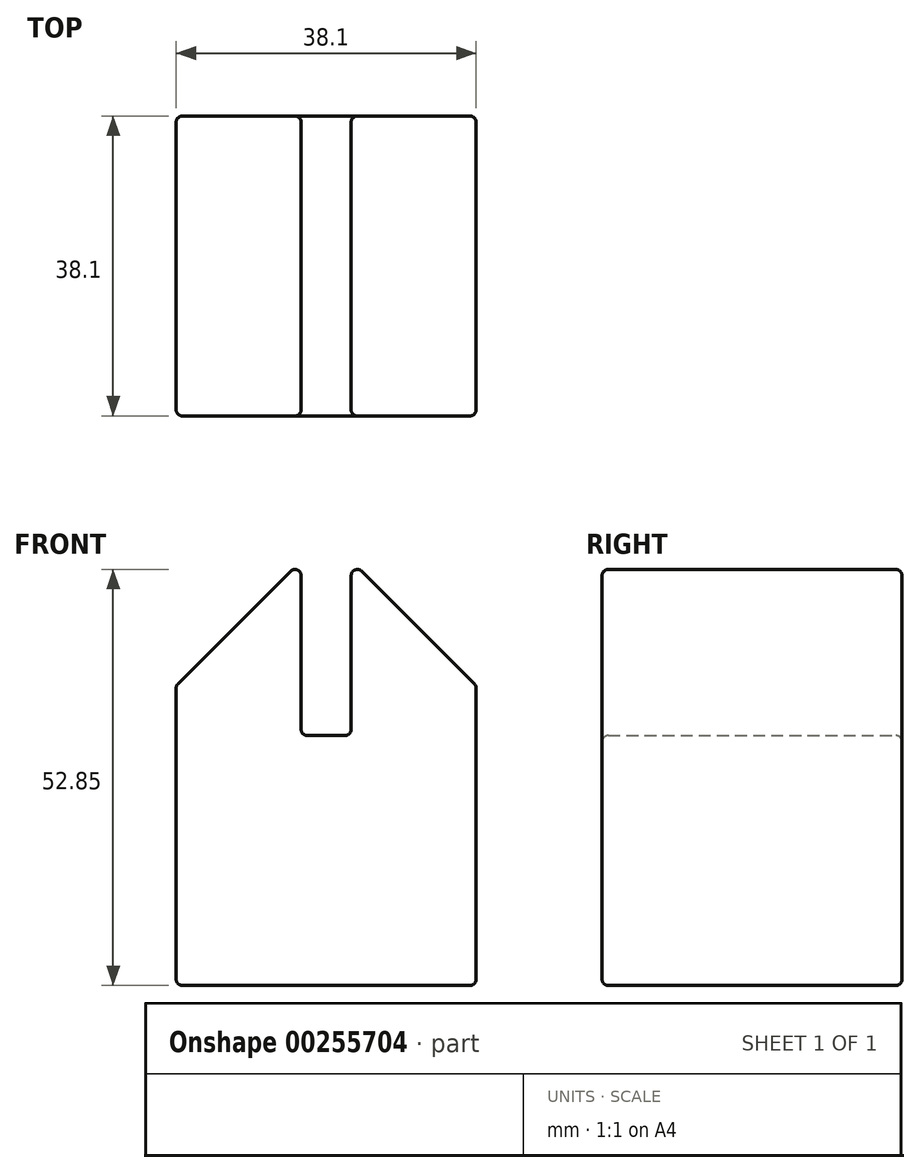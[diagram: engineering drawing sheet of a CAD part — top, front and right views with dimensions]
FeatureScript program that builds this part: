
annotation { "Feature Type Name" : "Feature", "Feature Type Description" : "" }
export const myFeature = defineFeature(function(context is Context, id is Id, definition is map)
    precondition{}
    {
        {
            var Q0;
            Q0=qCreatedBy(makeId("Front.planeOp"),FACE);
            var sketch = newSketch(context, id + "F0", { "sketchPlane" : qUnion([Q0])});
            skLineSegment(sketch, "E0", {"start": v(0, 0) * mm, "end": v(0, 38.1) * mm});
            skLineSegment(sketch, "E1", {"start": v(38.1, 38.1) * mm, "end": v(38.1, 0) * mm});
            skLineSegment(sketch, "E2", {"start": v(38.1, 0) * mm, "end": v(0, 0) * mm});
            skLineSegment(sketch, "E3", {"start": v(0, 38.1) * mm, "end": v(38.1, 38.1) * mm, "construction": true});
            skLineSegment(sketch, "E4", {"start": v(19.05, 38.1) * mm, "end": v(19.05, 57.15) * mm, "construction": true});
            skLineSegment(sketch, "E5", {"start": v(0, 38.1) * mm, "end": v(19.05, 57.15) * mm});
            skLineSegment(sketch, "E6", {"start": v(38.1, 38.1) * mm, "end": v(19.05, 57.15) * mm});
            skLineSegment(sketch, "E7", {"start": v(19.05, 38.1) * mm, "end": v(19.05, 31.75) * mm, "construction": true});
            skLineSegment(sketch, "E8", {"start": v(19.05, 31.75) * mm, "end": v(0, 31.75) * mm, "construction": true});
            skPoint(sketch, "E9", {"position": v(15.87, 31.75) * mm});
            skLineSegment(sketch, "E10", {"start": v(15.87, 31.75) * mm, "end": v(15.88, 53.97) * mm});
            skLineSegment(sketch, "E11", {"start": v(15.87, 31.75) * mm, "end": v(19.05, 31.75) * mm});
            skLineSegment(sketch, "E12.MirrorCS", {"start": v(22.23, 31.75) * mm, "end": v(19.05, 31.75) * mm});
            skPoint(sketch, "E13.MirrorP", {"position": v(22.23, 31.75) * mm});
            skLineSegment(sketch, "E14.MirrorCS", {"start": v(22.23, 31.75) * mm, "end": v(22.23, 53.97) * mm});
            skSolve(sketch);
        }
        {
            var Q0;
            Q0=makeQuery(id+"F0.imprint","IMPRINT",FACE,{"disambiguationData":[TD([[makeQuery(id+"F0.imprint","IMPRINT",EDGE,{"derivedFrom":sQuery(id+"F0.wireOp",EDGE,"E0")}),-1.0]])]});
            extrude(context, id + "F1", {"entities" : qUnion([Q0]), "depth" : 38.1 * mm});
        }
        {
            var Q0;
            Q0=makeQuery(id+"F1.opExtrude","CAP_EDGE",EDGE,{"disambiguationData":[OSD([sQuery(id+"F0.wireOp",EDGE,"E6")])],"isStart":false});
            var Q1;
            Q1=makeQuery(id+"F1.opExtrude","CAP_EDGE",EDGE,{"disambiguationData":[OSD([sQuery(id+"F0.wireOp",EDGE,"E6")])],"isStart":true});
            var Q2;
            Q2=makeQuery(id+"F1.opExtrude","SWEPT_EDGE",EDGE,{"disambiguationData":[OSD([sQuery(id+"F0.wireOp",EDGE,"E6"),sQuery(id+"F0.wireOp",EDGE,"E14.MirrorCS")])]});
            var Q3;
            Q3=makeQuery(id+"F1.opExtrude","SWEPT_EDGE",EDGE,{"disambiguationData":[OSD([sQuery(id+"F0.wireOp",EDGE,"E5"),sQuery(id+"F0.wireOp",EDGE,"E10")])]});
            var Q4;
            Q4=makeQuery(id+"F1.opExtrude","SWEPT_EDGE",EDGE,{"disambiguationData":[OSD([sQuery(id+"F0.wireOp",EDGE,"E10"),sQuery(id+"F0.wireOp",EDGE,"E11")])]});
            var Q5;
            Q5=makeQuery(id+"F1.opExtrude","SWEPT_EDGE",EDGE,{"disambiguationData":[OSD([sQuery(id+"F0.wireOp",EDGE,"E1"),sQuery(id+"F0.wireOp",EDGE,"E2")])]});
            var Q6;
            Q6=makeQuery(id+"F1.opExtrude","SWEPT_EDGE",EDGE,{"disambiguationData":[OSD([sQuery(id+"F0.wireOp",EDGE,"E1"),sQuery(id+"F0.wireOp",EDGE,"E6")])]});
            var Q7;
            Q7=makeQuery(id+"F1.opExtrude","SWEPT_EDGE",EDGE,{"disambiguationData":[OSD([sQuery(id+"F0.wireOp",EDGE,"E0"),sQuery(id+"F0.wireOp",EDGE,"E5")])]});
            var Q8;
            Q8=makeQuery(id+"F1.opExtrude","CAP_EDGE",EDGE,{"disambiguationData":[OSD([sQuery(id+"F0.wireOp",EDGE,"E5")])],"isStart":false});
            var Q9;
            Q9=makeQuery(id+"F1.opExtrude","CAP_EDGE",EDGE,{"disambiguationData":[OSD([sQuery(id+"F0.wireOp",EDGE,"E5")])],"isStart":true});
            var Q10;
            Q10=makeQuery(id+"F1.opExtrude","CAP_EDGE",EDGE,{"disambiguationData":[OSD([sQuery(id+"F0.wireOp",EDGE,"E2")])],"isStart":false});
            var Q11;
            Q11=makeQuery(id+"F1.opExtrude","CAP_EDGE",EDGE,{"disambiguationData":[OSD([sQuery(id+"F0.wireOp",EDGE,"E1")])],"isStart":false});
            var Q12;
            Q12=makeQuery(id+"F1.opExtrude","CAP_EDGE",EDGE,{"disambiguationData":[OSD([sQuery(id+"F0.wireOp",EDGE,"E2")])],"isStart":true});
            var Q13;
            Q13=makeQuery(id+"F1.opExtrude","CAP_EDGE",EDGE,{"disambiguationData":[OSD([sQuery(id+"F0.wireOp",EDGE,"E11"),sQuery(id+"F0.wireOp",EDGE,"E12.MirrorCS")])],"isStart":false});
            var Q14;
            Q14=makeQuery(id+"F1.opExtrude","CAP_EDGE",EDGE,{"disambiguationData":[OSD([sQuery(id+"F0.wireOp",EDGE,"E10")])],"isStart":true});
            var Q15;
            Q15=makeQuery(id+"F1.opExtrude","CAP_EDGE",EDGE,{"disambiguationData":[OSD([sQuery(id+"F0.wireOp",EDGE,"E10")])],"isStart":false});
            var Q16;
            Q16=makeQuery(id+"F1.opExtrude","CAP_EDGE",EDGE,{"disambiguationData":[OSD([sQuery(id+"F0.wireOp",EDGE,"E11"),sQuery(id+"F0.wireOp",EDGE,"E12.MirrorCS")])],"isStart":true});
            var Q17;
            Q17=makeQuery(id+"F1.opExtrude","CAP_EDGE",EDGE,{"disambiguationData":[OSD([sQuery(id+"F0.wireOp",EDGE,"E14.MirrorCS")])],"isStart":false});
            var Q18;
            Q18=makeQuery(id+"F1.opExtrude","CAP_EDGE",EDGE,{"disambiguationData":[OSD([sQuery(id+"F0.wireOp",EDGE,"E14.MirrorCS")])],"isStart":true});
            var Q19;
            Q19=makeQuery(id+"F1.opExtrude","CAP_EDGE",EDGE,{"disambiguationData":[OSD([sQuery(id+"F0.wireOp",EDGE,"E1")])],"isStart":true});
            var Q20;
            Q20=makeQuery(id+"F1.opExtrude","CAP_EDGE",EDGE,{"disambiguationData":[OSD([sQuery(id+"F0.wireOp",EDGE,"E0")])],"isStart":false});
            var Q21;
            Q21=makeQuery(id+"F1.opExtrude","CAP_EDGE",EDGE,{"disambiguationData":[OSD([sQuery(id+"F0.wireOp",EDGE,"E0")])],"isStart":true});
            var Q22;
            Q22=makeQuery(id+"F1.opExtrude","SWEPT_EDGE",EDGE,{"disambiguationData":[OSD([sQuery(id+"F0.wireOp",EDGE,"E12.MirrorCS"),sQuery(id+"F0.wireOp",EDGE,"E14.MirrorCS")])]});
            var Q23;
            Q23=makeQuery(id+"F1.opExtrude","SWEPT_EDGE",EDGE,{"disambiguationData":[OSD([sQuery(id+"F0.wireOp",EDGE,"E0"),sQuery(id+"F0.wireOp",EDGE,"E2")])]});
            fillet(context, id + "F2", {"entities" : qUnion([Q0, Q1, Q2, Q3, Q4, Q5, Q6, Q7, Q8, Q9, Q10, Q11, Q12, Q13, Q14, Q15, Q16, Q17, Q18, Q19, Q20, Q21, Q22, Q23]), "radius" : 0.8 * mm, "tangentPropagation" : true, "allowEdgeOverflow" : false});
        }
    });
